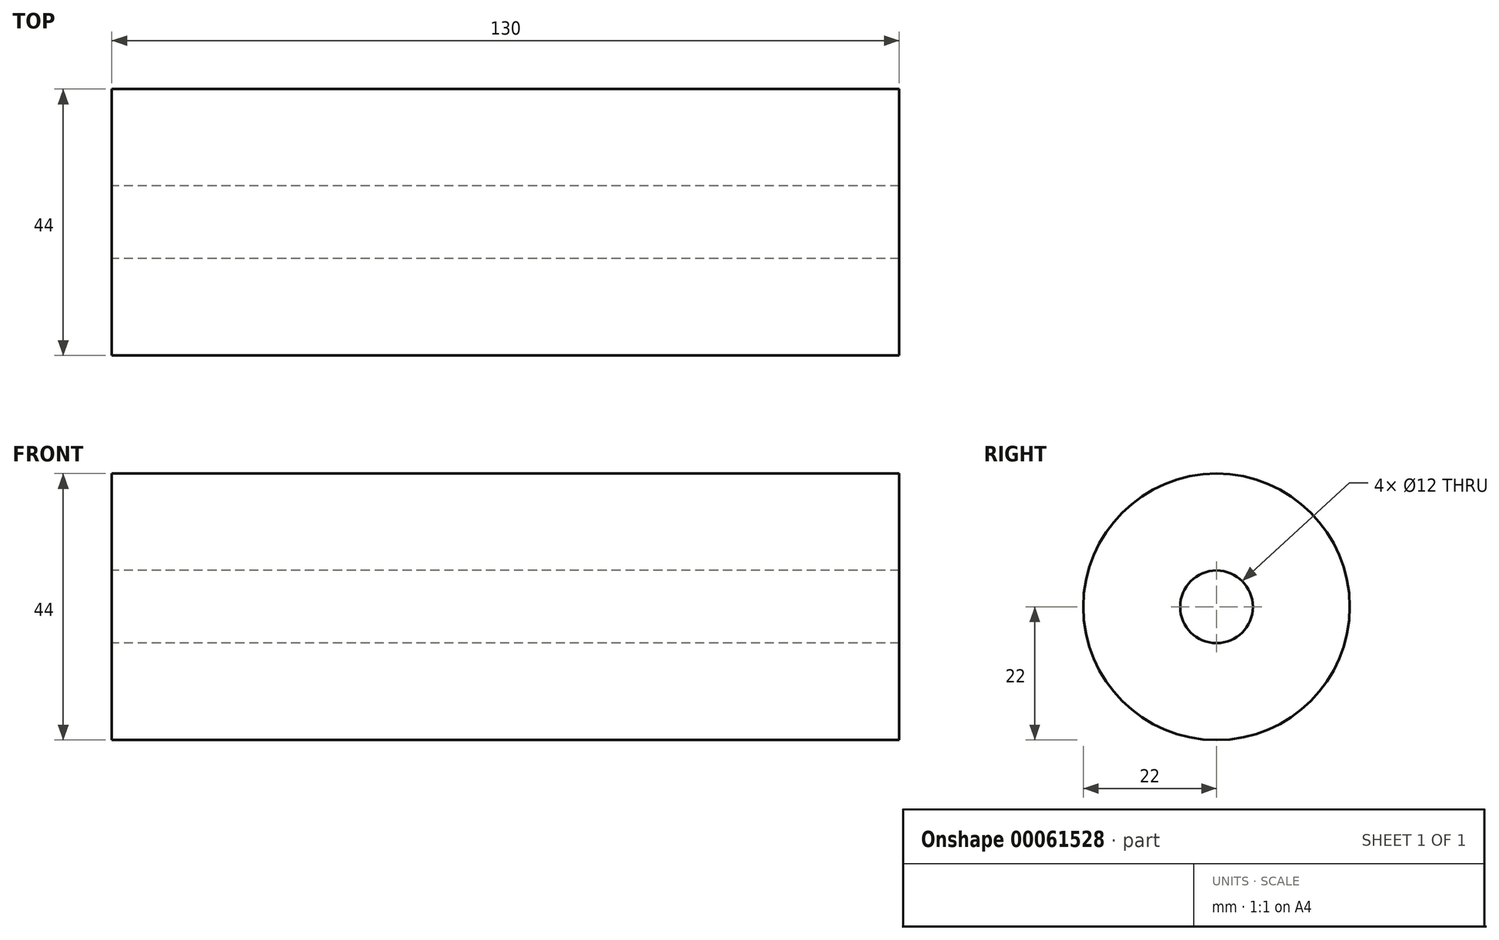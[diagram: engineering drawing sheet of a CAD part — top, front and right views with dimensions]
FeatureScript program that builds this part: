
annotation { "Feature Type Name" : "Feature", "Feature Type Description" : "" }
export const myFeature = defineFeature(function(context is Context, id is Id, definition is map)
    precondition{}
    {
        {
            var Q0;
            Q0=qCreatedBy(makeId("Front.planeOp"),FACE);
            var sketch = newSketch(context, id + "F0", { "sketchPlane" : qUnion([Q0])});
            skLineSegment(sketch, "E0", {"start": v(0, 22) * mm, "end": v(0, 6) * mm});
            skLineSegment(sketch, "E1", {"start": v(0, 6) * mm, "end": v(130, 6) * mm});
            skLineSegment(sketch, "E2", {"start": v(130, 6) * mm, "end": v(130, 22) * mm});
            skLineSegment(sketch, "E3", {"start": v(130, 22) * mm, "end": v(0, 22) * mm});
            skLineSegment(sketch, "E4", {"start": v(0, 0) * mm, "end": v(130, 0) * mm, "construction": true});
            skPoint(sketch, "E4.endSnap0", {"position": v(130, 14) * mm});
            skSolve(sketch);
        }
        {
            var Q0;
            Q0=makeQuery(id+"F0.imprint","IMPRINT",FACE,{"disambiguationData":[TD([[makeQuery(id+"F0.imprint","IMPRINT",EDGE,{"derivedFrom":sQuery(id+"F0.wireOp",EDGE,"E0")}),1.0]])]});
            var Q1;
            Q1=sQuery(id+"F0.wireOp",EDGE,"E4");
            revolve(context, id + "F1", {"entities" : qUnion([Q0]), "axis" : qUnion([Q1]), "revolveType" : RevolveType.FULL});
        }
    });
